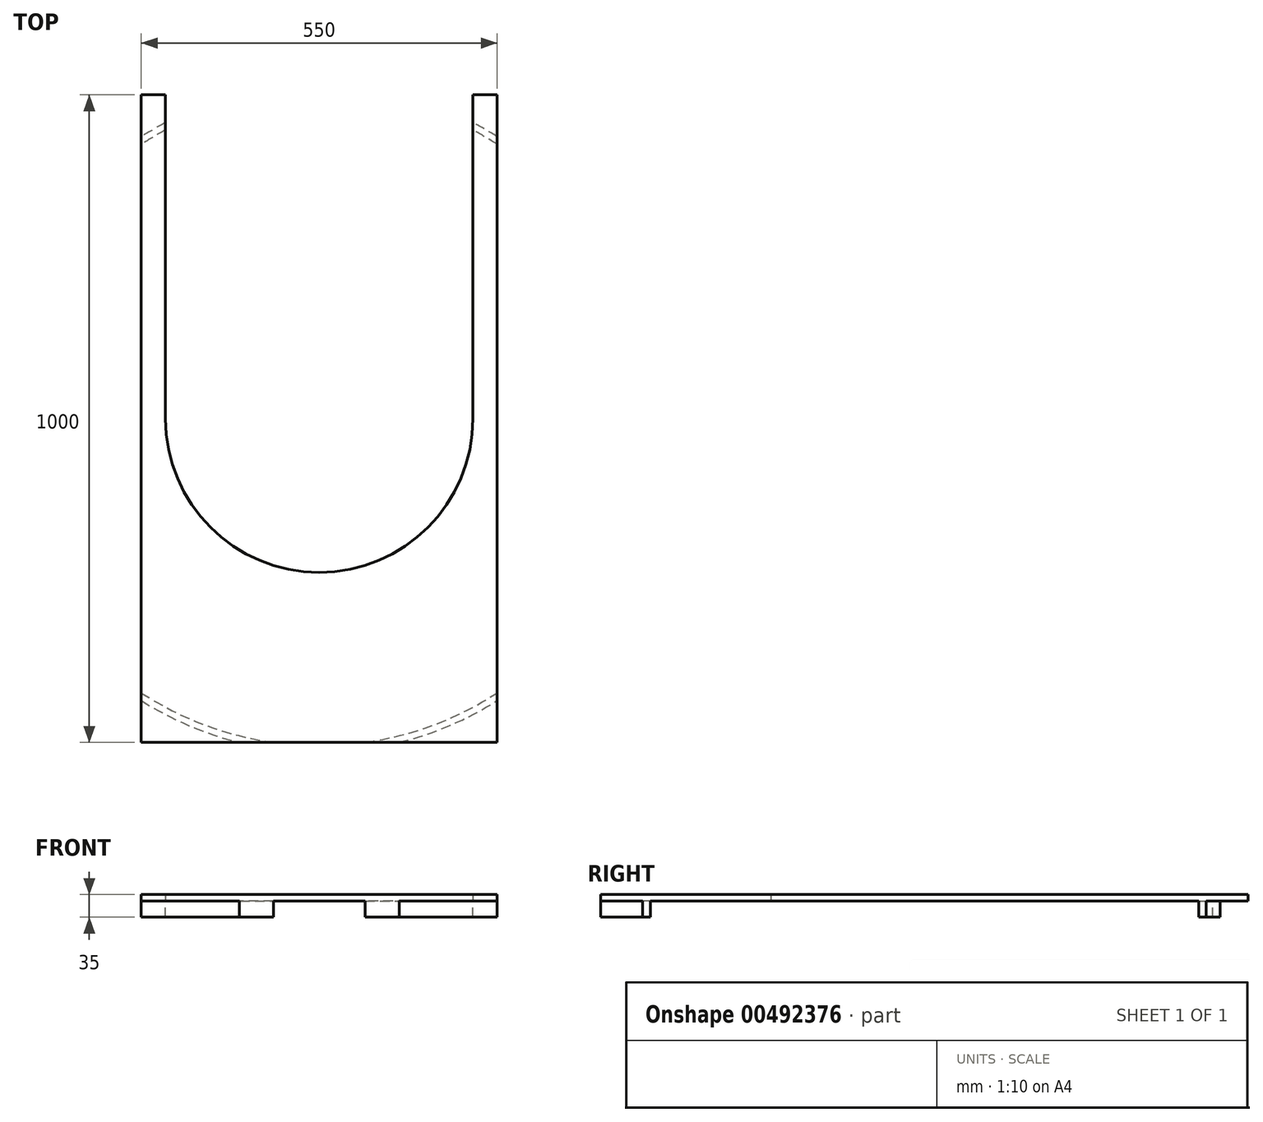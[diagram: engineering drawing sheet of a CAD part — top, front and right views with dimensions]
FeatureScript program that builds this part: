
annotation { "Feature Type Name" : "Feature", "Feature Type Description" : "" }
export const myFeature = defineFeature(function(context is Context, id is Id, definition is map)
    precondition{}
    {
        {
            var Q0;
            Q0=qCreatedBy(makeId("Top.planeOp"),FACE);
            var sketch = newSketch(context, id + "F0", { "sketchPlane" : qUnion([Q0])});
            skArc(sketch, "E0", {"start": v(-237.5, 0) * mm, "mid": v(0, -237.5) * mm, "end": v(237.5, 0) * mm});
            skLineSegment(sketch, "E1.bottom", {"start": v(-275, 500) * mm, "end": v(-237.5, 500) * mm});
            skLineSegment(sketch, "E1.top", {"start": v(-275, -500) * mm, "end": v(275, -500) * mm});
            skLineSegment(sketch, "E1.left", {"start": v(-275, 500) * mm, "end": v(-275, -500) * mm});
            skLineSegment(sketch, "E1.right", {"start": v(275, 500) * mm, "end": v(275, -500) * mm});
            skLineSegment(sketch, "E2", {"start": v(-237.5, 0) * mm, "end": v(-237.5, 500) * mm});
            skLineSegment(sketch, "E3", {"start": v(237.5, 0) * mm, "end": v(237.5, 500) * mm});
            skLineSegment(sketch, "E4.trimOffspring", {"start": v(237.5, 500) * mm, "end": v(275, 500) * mm});
            skSolve(sketch);
        }
        {
            var Q0;
            Q0=makeQuery(id+"F0.imprint","IMPRINT",FACE,{"disambiguationData":[TD([[makeQuery(id+"F0.imprint","IMPRINT",EDGE,{"derivedFrom":sQuery(id+"F0.wireOp",EDGE,"E0")}),-1.0]])]});
            extrude(context, id + "F1", {"entities" : qUnion([Q0]), "depth" : 10 * mm, "offsetDistance" : 25 * mm});
        }
        {
            var Q0;
            Q0=makeQuery(id+"F1.opExtrude","CAP_FACE",FACE,{"disambiguationData":[OSD([sQuery(id+"F0.wireOp",EDGE,"E0"),sQuery(id+"F0.wireOp",EDGE,"E1.bottom"),sQuery(id+"F0.wireOp",EDGE,"E1.top"),sQuery(id+"F0.wireOp",EDGE,"E1.left"),sQuery(id+"F0.wireOp",EDGE,"E1.right"),sQuery(id+"F0.wireOp",EDGE,"E2"),sQuery(id+"F0.wireOp",EDGE,"E3"),sQuery(id+"F0.wireOp",EDGE,"E4.trimOffspring")])],"isStart":true});
            var sketch = newSketch(context, id + "F2", { "sketchPlane" : qUnion([Q0])});
            skArc(sketch, "E5", {"start": v(-70.89, 500) * mm, "mid": v(-177.12, 472.92) * mm, "end": v(-275, 423.56) * mm});
            skArc(sketch, "E6", {"start": v(-123.39, 500) * mm, "mid": v(-201.8, 473.82) * mm, "end": v(-275, 435.43) * mm});
            skLineSegment(sketch, "E7", {"start": v(237.5, -445.67) * mm, "end": v(237.5, -456.97) * mm});
            skLineSegment(sketch, "E8", {"start": v(275, -435.43) * mm, "end": v(275, -423.56) * mm});
            skLineSegment(sketch, "E9", {"start": v(-237.5, -456.97) * mm, "end": v(-237.5, -445.67) * mm});
            skLineSegment(sketch, "E10", {"start": v(-275, -435.43) * mm, "end": v(-275, -423.56) * mm});
            skLineSegment(sketch, "E11", {"start": v(-275, 423.56) * mm, "end": v(-275, 435.43) * mm});
            skLineSegment(sketch, "E12", {"start": v(-123.39, 500) * mm, "end": v(-70.89, 500) * mm});
            skLineSegment(sketch, "E13.trimOffspring", {"start": v(70.89, 500) * mm, "end": v(123.39, 500) * mm});
            skArc(sketch, "E14.trimOffspring", {"start": v(-275, -423.56) * mm, "mid": v(-256.49, -435.02) * mm, "end": v(-237.5, -445.67) * mm});
            skArc(sketch, "E15.trimOffspring", {"start": v(-275, -435.43) * mm, "mid": v(-256.48, -446.6) * mm, "end": v(-237.5, -456.97) * mm});
            skArc(sketch, "E16.trimOffspring", {"start": v(237.5, -456.97) * mm, "mid": v(256.48, -446.6) * mm, "end": v(275, -435.43) * mm});
            skArc(sketch, "E17.trimOffspring", {"start": v(237.5, -445.67) * mm, "mid": v(256.49, -435.02) * mm, "end": v(275, -423.56) * mm});
            skLineSegment(sketch, "E18", {"start": v(275, 423.56) * mm, "end": v(275, 435.43) * mm});
            skArc(sketch, "E19.trimOffspring", {"start": v(275, 435.43) * mm, "mid": v(201.8, 473.82) * mm, "end": v(123.39, 500) * mm});
            skArc(sketch, "E20.trimOffspring", {"start": v(275, 423.56) * mm, "mid": v(177.12, 472.92) * mm, "end": v(70.89, 500) * mm});
            skSolve(sketch);
        }
        {
            var Q0;
            Q0 = qSketchRegion(id + "F2", true);
            extrude(context, id + "F3", {"entities" : qUnion([Q0]), "operationType" : NewBodyOperationType.ADD, "depth" : 25 * mm, "offsetDistance" : 25 * mm});
        }
    });
